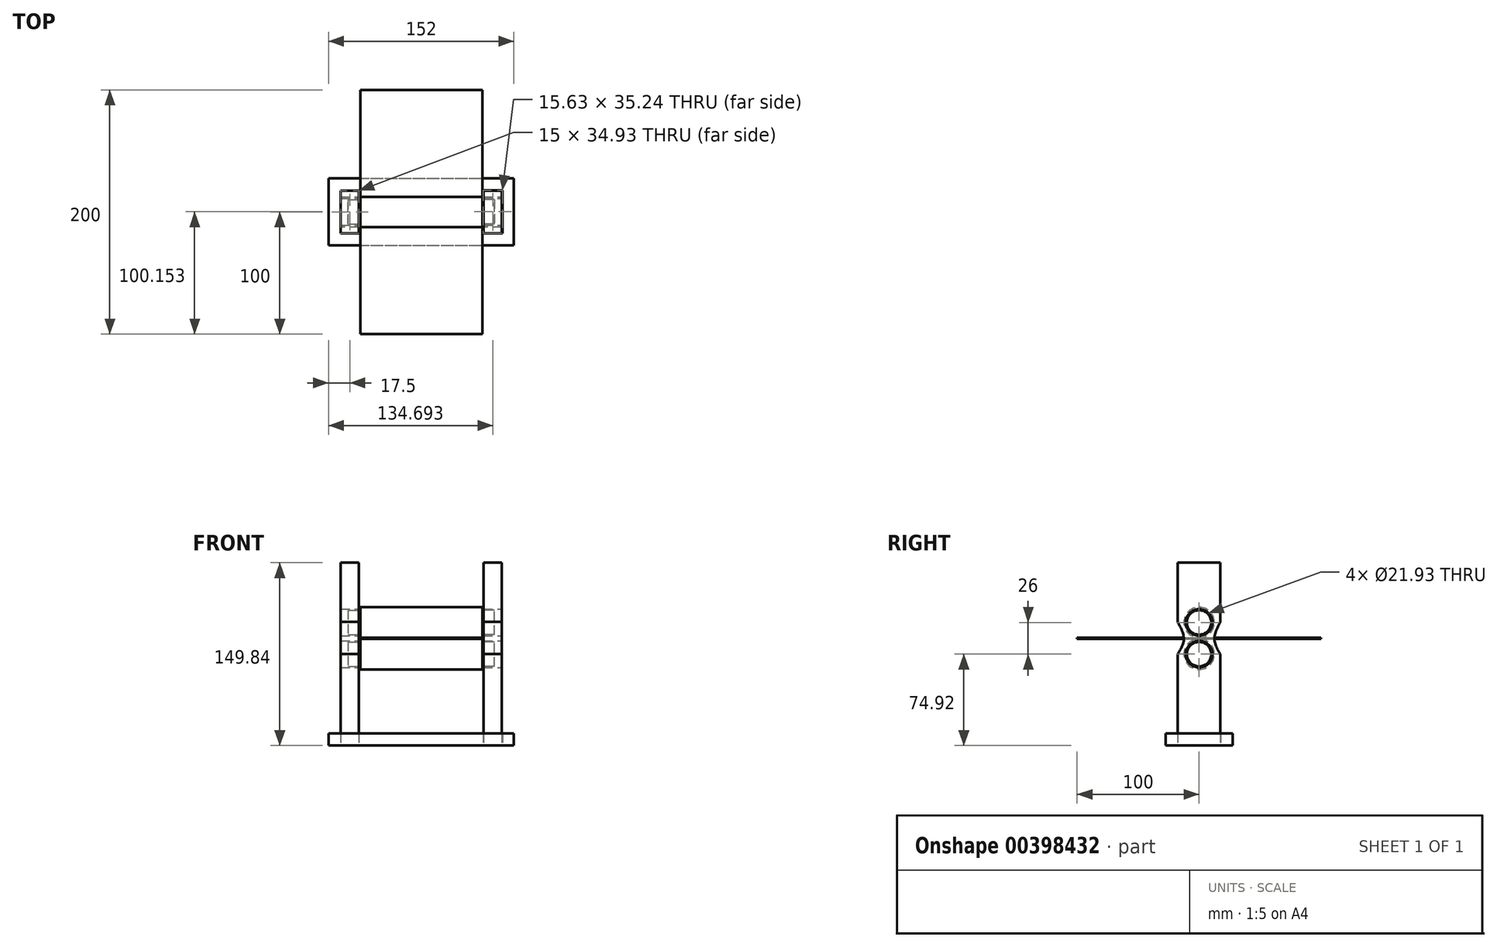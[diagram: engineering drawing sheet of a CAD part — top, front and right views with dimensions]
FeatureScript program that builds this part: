
annotation { "Feature Type Name" : "Feature", "Feature Type Description" : "" }
export const myFeature = defineFeature(function(context is Context, id is Id, definition is map)
    precondition{}
    {
        {
            var Q0;
            Q0=qCreatedBy(makeId("Right.planeOp"),FACE);
            var sketch = newSketch(context, id + "F0", { "sketchPlane" : qUnion([Q0])});
            skCircle(sketch, "E0", {"center": v(0, 0) * mm, "radius": 12.5 * mm});
            skSolve(sketch);
        }
        {
            var Q0;
            Q0 = qSketchRegion(id + "F0", true);
            extrude(context, id + "F1", {"entities" : qUnion([Q0]), "depth" : 100 * mm});
        }
        {
            var Q0;
            Q0=makeQuery(id+"F1.opExtrude","CAP_FACE",FACE,{"disambiguationData":[OSD([sQuery(id+"F0.wireOp",EDGE,"E0")])],"isStart":false});
            var sketch = newSketch(context, id + "F2", { "sketchPlane" : qUnion([Q0])});
            skCircle(sketch, "E1", {"center": v(0, 0) * mm, "radius": 10 * mm});
            skSolve(sketch);
        }
        {
            var Q0;
            Q0=makeQuery(id+"F2.imprint","IMPRINT",FACE,{"disambiguationData":[TD([[makeQuery(id+"F2.imprint","IMPRINT",EDGE,{"derivedFrom":sQuery(id+"F2.wireOp",EDGE,"E1")}),1.0]])]});
            extrude(context, id + "F3", {"entities" : qUnion([Q0]), "operationType" : NewBodyOperationType.ADD, "depth" : 10 * mm});
        }
        {
            var Q0;
            Q0=makeQuery(id+"F1.opExtrude","CAP_FACE",FACE,{"disambiguationData":[OSD([sQuery(id+"F0.wireOp",EDGE,"E0")])],"isStart":true});
            var sketch = newSketch(context, id + "F4", { "sketchPlane" : qUnion([Q0])});
            skCircle(sketch, "E2", {"center": v(0, 0) * mm, "radius": 10 * mm});
            skSolve(sketch);
        }
        {
            var Q0;
            Q0 = qSketchRegion(id + "F4", true);
            extrude(context, id + "F5", {"entities" : qUnion([Q0]), "operationType" : NewBodyOperationType.ADD, "depth" : 10 * mm});
        }
        {
            var Q0;
            Q0=makeQuery(id+"F1.opExtrude","SWEPT_BODY",BODY,{"disambiguationData":[OSD([sQuery(id+"F0.wireOp",EDGE,"E0")])]});
            transform(context, id + "F6", {"entities" : qUnion([Q0]), "transformType" : TransformType.TRANSLATION_3D, "dx" : 0 * mm, "dy" : 0 * mm, "dz" : 26 * mm, "makeCopy" : true});
        }
        {
            var Q0;
            Q0=qCreatedBy(makeId("Right.planeOp"),FACE);
            var sketch = newSketch(context, id + "F7", { "sketchPlane" : qUnion([Q0])});
            skLineSegment(sketch, "E3.bottom", {"start": v(-17.47, 74.92) * mm, "end": v(17.47, 74.92) * mm});
            skLineSegment(sketch, "E3.top", {"start": v(-17.47, -74.92) * mm, "end": v(17.47, -74.92) * mm});
            skLineSegment(sketch, "E3.left", {"start": v(-17.47, 74.92) * mm, "end": v(-17.47, 26.35) * mm});
            skLineSegment(sketch, "E3.right", {"start": v(17.47, 74.92) * mm, "end": v(17.47, 26.35) * mm});
            skFitSpline(sketch, "E4", {"points": [v(17.47, 26.35) * mm, v(12.5, 12.5) * mm, v(17.47, 0) * mm], "startDerivative": vector(-14.8, -27.48) * mm, "endDerivative": vector(15.02, -25.2) * mm});
            skLineSegment(sketch, "E5.trimOffspring", {"start": v(17.47, 0) * mm, "end": v(17.47, -74.92) * mm});
            skFitSpline(sketch, "E6.MirrorCS", {"points": [v(-17.47, 26.35) * mm, v(-12.5, 12.5) * mm, v(-17.47, 0) * mm], "startDerivative": vector(14.8, -27.48) * mm, "endDerivative": vector(-15.02, -25.2) * mm});
            skLineSegment(sketch, "E7.trimOffspring", {"start": v(-17.47, 0) * mm, "end": v(-17.47, -74.92) * mm});
            skCircle(sketch, "E8", {"center": v(0, 0) * mm, "radius": 10.96 * mm});
            skPoint(sketch, "E9", {"position": v(0, 13) * mm});
            skCircle(sketch, "E10.MirrorC", {"center": v(0, 26) * mm, "radius": 10.96 * mm});
            skSolve(sketch);
        }
        {
            var Q0;
            Q0=makeQuery(id+"F7.imprint","IMPRINT",FACE,{"disambiguationData":[TD([[makeQuery(id+"F7.imprint","IMPRINT",EDGE,{"derivedFrom":sQuery(id+"F7.wireOp",EDGE,"E3.bottom")}),-1.0]])]});
            extrude(context, id + "F8", {"entities" : qUnion([Q0]), "oppositeDirection" : true, "depth" : 15 * mm});
        }
        {
            var Q0;
            Q0=makeQuery(id+"F8.opExtrude","SWEPT_BODY",BODY,{"disambiguationData":[OSD([sQuery(id+"F7.wireOp",EDGE,"E3.bottom"),sQuery(id+"F7.wireOp",EDGE,"E3.top"),sQuery(id+"F7.wireOp",EDGE,"E3.left"),sQuery(id+"F7.wireOp",EDGE,"E3.right"),sQuery(id+"F7.wireOp",EDGE,"E4"),sQuery(id+"F7.wireOp",EDGE,"E5.trimOffspring"),sQuery(id+"F7.wireOp",EDGE,"E6.MirrorCS"),sQuery(id+"F7.wireOp",EDGE,"E7.trimOffspring"),sQuery(id+"F7.wireOp",EDGE,"E8"),sQuery(id+"F7.wireOp",EDGE,"E10.MirrorC")])]});
            transform(context, id + "F9", {"entities" : qUnion([Q0]), "transformType" : TransformType.TRANSLATION_3D, "dx" : 2 * mm, "dy" : 0 * mm, "dz" : 0 * mm, "makeCopy" : false});
        }
        {
            var Q0;
            Q0=makeQuery(id+"F8.opExtrude","SWEPT_BODY",BODY,{"disambiguationData":[OSD([sQuery(id+"F7.wireOp",EDGE,"E3.bottom"),sQuery(id+"F7.wireOp",EDGE,"E3.top"),sQuery(id+"F7.wireOp",EDGE,"E3.left"),sQuery(id+"F7.wireOp",EDGE,"E3.right"),sQuery(id+"F7.wireOp",EDGE,"E4"),sQuery(id+"F7.wireOp",EDGE,"E5.trimOffspring"),sQuery(id+"F7.wireOp",EDGE,"E6.MirrorCS"),sQuery(id+"F7.wireOp",EDGE,"E7.trimOffspring"),sQuery(id+"F7.wireOp",EDGE,"E8"),sQuery(id+"F7.wireOp",EDGE,"E10.MirrorC")])]});
            transform(context, id + "F10", {"entities" : qUnion([Q0]), "transformType" : TransformType.TRANSLATION_3D, "dx" : -3 * mm, "dy" : 0 * mm, "dz" : 0 * mm, "makeCopy" : false});
        }
        {
            var Q0;
            Q0=makeQuery(id+"F8.opExtrude","SWEPT_BODY",BODY,{"disambiguationData":[OSD([sQuery(id+"F7.wireOp",EDGE,"E3.bottom"),sQuery(id+"F7.wireOp",EDGE,"E3.top"),sQuery(id+"F7.wireOp",EDGE,"E3.left"),sQuery(id+"F7.wireOp",EDGE,"E3.right"),sQuery(id+"F7.wireOp",EDGE,"E4"),sQuery(id+"F7.wireOp",EDGE,"E5.trimOffspring"),sQuery(id+"F7.wireOp",EDGE,"E6.MirrorCS"),sQuery(id+"F7.wireOp",EDGE,"E7.trimOffspring"),sQuery(id+"F7.wireOp",EDGE,"E8"),sQuery(id+"F7.wireOp",EDGE,"E10.MirrorC")])]});
            transform(context, id + "F11", {"entities" : qUnion([Q0]), "transformType" : TransformType.TRANSLATION_3D, "dx" : 117 * mm, "dy" : 0 * mm, "dz" : 0 * mm, "makeCopy" : true});
        }
        {
            var Q0;
            Q0=makeQuery(id+"F8.opExtrude","SWEPT_FACE",FACE,{"disambiguationData":[OSD([sQuery(id+"F7.wireOp",EDGE,"E3.top")])]});
            var sketch = newSketch(context, id + "F12", { "sketchPlane" : qUnion([Q0])});
            skLineSegment(sketch, "E11.bottom", {"start": v(-26, 27.47) * mm, "end": v(126, 27.47) * mm});
            skLineSegment(sketch, "E11.top", {"start": v(-26, -27.47) * mm, "end": v(126, -27.47) * mm});
            skLineSegment(sketch, "E11.left", {"start": v(-26, 27.47) * mm, "end": v(-26, -27.47) * mm});
            skLineSegment(sketch, "E11.right", {"start": v(126, 27.47) * mm, "end": v(126, -27.47) * mm});
            skLineSegment(sketch, "E12.bottom", {"start": v(116.5, 17.47) * mm, "end": v(100.88, 17.47) * mm});
            skLineSegment(sketch, "E12.top", {"start": v(116.5, -17.77) * mm, "end": v(100.88, -17.77) * mm});
            skLineSegment(sketch, "E12.left", {"start": v(116.5, 17.47) * mm, "end": v(116.5, -17.77) * mm});
            skLineSegment(sketch, "E12.right", {"start": v(100.88, 17.47) * mm, "end": v(100.88, -17.77) * mm});
            skLineSegment(sketch, "E13.bottom", {"start": v(-16, 17.47) * mm, "end": v(-1, 17.47) * mm});
            skLineSegment(sketch, "E13.top", {"start": v(-16, -17.47) * mm, "end": v(-1, -17.47) * mm});
            skLineSegment(sketch, "E13.left", {"start": v(-16, 17.47) * mm, "end": v(-16, -17.47) * mm});
            skLineSegment(sketch, "E13.right", {"start": v(-1, 17.47) * mm, "end": v(-1, -17.47) * mm});
            skSolve(sketch);
        }
        {
            var Q0;
            Q0=makeQuery(id+"F12.imprint","IMPRINT",FACE,{"disambiguationData":[TD([[makeQuery(id+"F12.imprint","IMPRINT",EDGE,{"derivedFrom":sQuery(id+"F12.wireOp",EDGE,"E11.bottom")}),-1.0]])]});
            extrude(context, id + "F13", {"entities" : qUnion([Q0]), "oppositeDirection" : true, "depth" : 10 * mm});
        }
        {
            var Q0;
            Q0=qCreatedBy(makeId("Front.planeOp"),FACE);
            var sketch = newSketch(context, id + "F14", { "sketchPlane" : qUnion([Q0])});
            skLineSegment(sketch, "E14.bottom", {"start": v(0, 13.4) * mm, "end": v(100, 13.4) * mm});
            skLineSegment(sketch, "E14.top", {"start": v(0, 12.6) * mm, "end": v(100, 12.6) * mm});
            skLineSegment(sketch, "E14.left", {"start": v(0, 13.4) * mm, "end": v(0, 12.6) * mm});
            skLineSegment(sketch, "E14.right", {"start": v(100, 13.4) * mm, "end": v(100, 12.6) * mm});
            skSolve(sketch);
        }
        {
            var Q0;
            Q0 = qSketchRegion(id + "F14", true);
            extrude(context, id + "F15", {"entities" : qUnion([Q0]), "depth" : 200 * mm, "symmetric" : true});
        }
    });
